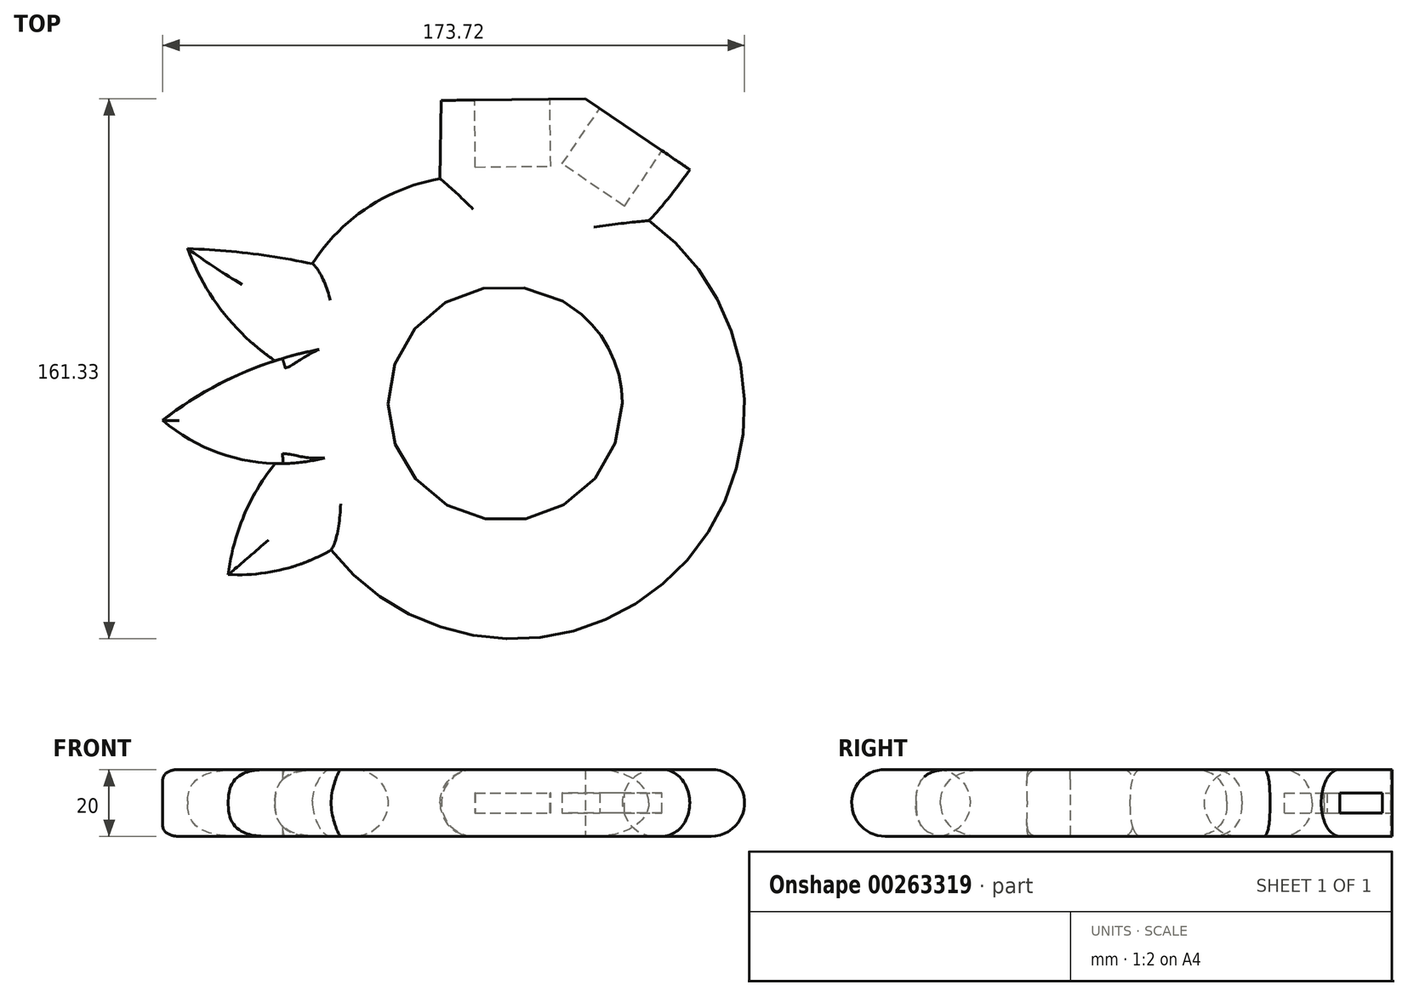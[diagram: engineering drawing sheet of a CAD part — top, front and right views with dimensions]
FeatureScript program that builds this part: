
annotation { "Feature Type Name" : "Feature", "Feature Type Description" : "" }
export const myFeature = defineFeature(function(context is Context, id is Id, definition is map)
    precondition{}
    {
        {
            var Q0;
            Q0=qCreatedBy(makeId("Top.planeOp"),FACE);
            var sketch = newSketch(context, id + "F0", { "sketchPlane" : qUnion([Q0])});
            skArc(sketch, "E0", {"start": v(-69.56, -48.3) * mm, "mid": v(-88.08, -45.25) * mm, "end": v(-106.8, -43.78) * mm});
            skArc(sketch, "E1", {"start": v(-106.8, -43.78) * mm, "mid": v(-96.39, -62.57) * mm, "end": v(-80.73, -77.27) * mm});
            skArc(sketch, "E2", {"start": v(-80.73, -77.27) * mm, "mid": v(-98.26, -84.7) * mm, "end": v(-114.23, -95.07) * mm});
            skArc(sketch, "E3", {"start": v(-114.23, -95.07) * mm, "mid": v(-98.6, -104.41) * mm, "end": v(-80.73, -107.98) * mm});
            skArc(sketch, "E4", {"start": v(-80.73, -107.98) * mm, "mid": v(-90.04, -123.58) * mm, "end": v(-94.69, -141.13) * mm});
            skArc(sketch, "E5", {"start": v(-94.69, -141.13) * mm, "mid": v(-78.8, -139.7) * mm, "end": v(-63.98, -133.8) * mm});
            skArc(sketch, "E6", {"start": v(-63.98, -133.8) * mm, "mid": v(40.14, -139.24) * mm, "end": v(30.94, -35.4) * mm});
            skArc(sketch, "E7", {"start": v(-31.41, -22.87) * mm, "mid": v(-53.17, -31.57) * mm, "end": v(-69.56, -48.3) * mm});
            skCircle(sketch, "E8", {"center": v(-12, -90) * mm, "radius": 35 * mm});
            skLineSegment(sketch, "E9", {"start": v(-12, -90) * mm, "end": v(-12, 0) * mm});
            skLineSegment(sketch, "E10", {"start": v(-12, 0) * mm, "end": v(0, 0) * mm});
            skLineSegment(sketch, "E11", {"start": v(-31.41, -22.87) * mm, "end": v(-12, 0) * mm});
            skLineSegment(sketch, "E12", {"start": v(-31.41, -22.87) * mm, "end": v(0, 0) * mm});
            skArc(sketch, "E13", {"start": v(30.94, -35.4) * mm, "mid": v(57.65, 8.29) * mm, "end": v(64.82, 58.99) * mm});
            skLineSegment(sketch, "E14", {"start": v(64.82, 42.9) * mm, "end": v(70.1, 125.75) * mm});
            skLineSegment(sketch, "E15", {"start": v(70.1, 125.75) * mm, "end": v(73.47, 146.99) * mm});
            skLineSegment(sketch, "E16", {"start": v(73.47, 146.99) * mm, "end": v(91.25, 150.97) * mm});
            skArc(sketch, "E17", {"start": v(93.55, 168.05) * mm, "mid": v(98.13, 170.3) * mm, "end": v(101.04, 174.5) * mm});
            skArc(sketch, "E18", {"start": v(101.04, 174.5) * mm, "mid": v(98.19, 178.86) * mm, "end": v(93.55, 181.22) * mm});
            skArc(sketch, "E19", {"start": v(91.25, 150.97) * mm, "mid": v(97.19, 153.5) * mm, "end": v(101.85, 157.96) * mm});
            skArc(sketch, "E20", {"start": v(101.85, 157.96) * mm, "mid": v(99.5, 164.5) * mm, "end": v(93.55, 168.05) * mm});
            skArc(sketch, "E21", {"start": v(93.55, 181.22) * mm, "mid": v(100.45, 185.24) * mm, "end": v(104.38, 192.2) * mm});
            skArc(sketch, "E22", {"start": v(16.27, 5.35) * mm, "mid": v(27.94, 20.47) * mm, "end": v(35.96, 37.8) * mm});
            skLineSegment(sketch, "E23", {"start": v(16.27, 5.35) * mm, "end": v(12.02, 0.97) * mm});
            skLineSegment(sketch, "E24", {"start": v(12.02, 54.47) * mm, "end": v(16.98, 220.58) * mm});
            skLineSegment(sketch, "E25", {"start": v(16.98, 220.58) * mm, "end": v(16.98, 230.48) * mm});
            skArc(sketch, "E26", {"start": v(20.74, 234.78) * mm, "mid": v(18.05, 233.34) * mm, "end": v(16.98, 230.48) * mm});
            skLineSegment(sketch, "E27", {"start": v(20.74, 234.78) * mm, "end": v(55.67, 234.78) * mm});
            skArc(sketch, "E28", {"start": v(55.67, 234.78) * mm, "mid": v(75.45, 242.82) * mm, "end": v(84, 262.38) * mm});
            skArc(sketch, "E29", {"start": v(84, 262.38) * mm, "mid": v(83.8, 275) * mm, "end": v(79.59, 286.9) * mm});
            skArc(sketch, "E30", {"start": v(79.59, 286.9) * mm, "mid": v(90.12, 305.47) * mm, "end": v(96.46, 325.87) * mm});
            skArc(sketch, "E31", {"start": v(96.46, 325.87) * mm, "mid": v(80.34, 314.22) * mm, "end": v(65.52, 300.95) * mm});
            skArc(sketch, "E32", {"start": v(65.52, 300.95) * mm, "mid": v(66.02, 314.82) * mm, "end": v(65.52, 328.68) * mm});
            skArc(sketch, "E33", {"start": v(41.86, 304.54) * mm, "mid": v(40.03, 315.53) * mm, "end": v(35.9, 325.87) * mm});
            skArc(sketch, "E34", {"start": v(35.9, 325.87) * mm, "mid": v(29.68, 316.4) * mm, "end": v(23.68, 306.81) * mm});
            skArc(sketch, "E35", {"start": v(23.68, 306.81) * mm, "mid": v(-21.12, 284.92) * mm, "end": v(-28, 235.53) * mm});
            skLineSegment(sketch, "E36", {"start": v(-31.41, -22.87) * mm, "end": v(-28, 235.53) * mm});
            skLineSegment(sketch, "E37", {"start": v(0, 0) * mm, "end": v(0, 302.13) * mm});
            skLineSegment(sketch, "E38", {"start": v(12.02, 0.97) * mm, "end": v(-31.41, -22.87) * mm});
            skLineSegment(sketch, "E39", {"start": v(0, 0) * mm, "end": v(12.02, 0.97) * mm});
            skLineSegment(sketch, "E40", {"start": v(12.02, 0.97) * mm, "end": v(30.94, -35.4) * mm});
            skLineSegment(sketch, "E41", {"start": v(64.82, 58.99) * mm, "end": v(46.6, 104.17) * mm});
            skLineSegment(sketch, "E42", {"start": v(12.02, 0.97) * mm, "end": v(12.02, 54.47) * mm});
            skLineSegment(sketch, "E43", {"start": v(-29.54, 119.27) * mm, "end": v(13.94, 118.7) * mm});
            skLineSegment(sketch, "E44", {"start": v(35.96, 37.8) * mm, "end": v(38.97, 138.47) * mm});
            skArc(sketch, "E45", {"start": v(104.38, 192.2) * mm, "mid": v(74.78, 206.52) * mm, "end": v(46.71, 189.39) * mm});
            skArc(sketch, "E46", {"start": v(46.71, 189.39) * mm, "mid": v(41.3, 164.16) * mm, "end": v(38.97, 138.47) * mm});
            skLineSegment(sketch, "E47", {"start": v(104.38, 192.2) * mm, "end": v(93.55, 181.22) * mm});
            skLineSegment(sketch, "E48", {"start": v(93.55, 168.05) * mm, "end": v(101.85, 157.96) * mm});
            skLineSegment(sketch, "E49", {"start": v(93.55, 181.22) * mm, "end": v(101.04, 174.5) * mm});
            skLineSegment(sketch, "E50", {"start": v(93.55, 168.05) * mm, "end": v(101.04, 174.5) * mm});
            skLineSegment(sketch, "E51", {"start": v(41.86, 304.54) * mm, "end": v(65.52, 328.68) * mm});
            skLineSegment(sketch, "E52", {"start": v(16.98, 230.48) * mm, "end": v(-28.07, 230.48) * mm});
            skLineSegment(sketch, "E53", {"start": v(12.02, 0.97) * mm, "end": v(-31.1, 0.49) * mm});
            skPoint(sketch, "E53.endSnap0", {"position": v(6.01, 0.49) * mm});
            skLineSegment(sketch, "E54", {"start": v(12.02, 0.97) * mm, "end": v(43.15, -20.17) * mm});
            skSolve(sketch);
        }
        {
            var Q0;
            {var subQ0=sQuery(id+"F0.wireOp",EDGE,"E38");var subQ1=sQuery(id+"F0.wireOp",EDGE,"E9");var subQ2=makeQuery(id+"F0.imprint","INTERSECT",VERTEX,{"derivedFrom":[subQ1,subQ0]});Q0=makeQuery(id+"F0.imprint","IMPRINT",FACE,{"disambiguationData":[TD([[makeQuery(id+"F0.imprint","IMPRINT",EDGE,{"disambiguationData":[TD([[subQ2,-1.0]])],"derivedFrom":subQ1}),1.0]])]});}
            var Q1;
            {var subQ0=sQuery(id+"F0.wireOp",EDGE,"E11");Q1=makeQuery(id+"F0.imprint","IMPRINT",FACE,{"disambiguationData":[TD([[makeQuery(id+"F0.imprint","IMPRINT",EDGE,{"derivedFrom":subQ0}),-1.0]])]});}
            var Q2;
            {var subQ0=sQuery(id+"F0.wireOp",EDGE,"E39");Q2=makeQuery(id+"F0.imprint","IMPRINT",FACE,{"disambiguationData":[TD([[makeQuery(id+"F0.imprint","IMPRINT",EDGE,{"derivedFrom":subQ0}),1.0]])]});}
            var Q3;
            Q3=makeQuery(id+"F0.imprint","IMPRINT",FACE,{"disambiguationData":[TD([[makeQuery(id+"F0.imprint","IMPRINT",EDGE,{"derivedFrom":sQuery(id+"F0.wireOp",EDGE,"E0")}),1.0]])]});
            var Q4;
            {var subQ5=sQuery(id+"F0.wireOp",EDGE,"E39");Q4=makeQuery(id+"F0.imprint","IMPRINT",FACE,{"disambiguationData":[TD([[makeQuery(id+"F0.imprint","IMPRINT",EDGE,{"derivedFrom":subQ5}),-1.0]])]});}
            var Q5;
            {var subQ2=sQuery(id+"F0.wireOp",EDGE,"E10");Q5=makeQuery(id+"F0.imprint","IMPRINT",FACE,{"disambiguationData":[TD([[makeQuery(id+"F0.imprint","IMPRINT",EDGE,{"derivedFrom":subQ2}),1.0]])]});}
            var Q6;
            {var subQ0=sQuery(id+"F0.wireOp",EDGE,"E10");Q6=makeQuery(id+"F0.imprint","IMPRINT",FACE,{"disambiguationData":[TD([[makeQuery(id+"F0.imprint","IMPRINT",EDGE,{"derivedFrom":subQ0}),-1.0]])]});}
            var Q7;
            {var subQ0=sQuery(id+"F0.wireOp",EDGE,"E40");Q7=makeQuery(id+"F0.imprint","IMPRINT",FACE,{"disambiguationData":[TD([[makeQuery(id+"F0.imprint","IMPRINT",EDGE,{"derivedFrom":subQ0}),1.0]])]});}
            extrude(context, id + "F1", {"entities" : qUnion([Q0, Q1, Q2, Q3, Q4, Q5, Q6, Q7]), "depth" : 20 * mm});
        }
        {
            var Q0;
            {var subQ1=sQuery(id+"F0.wireOp",EDGE,"E14");Q0=makeQuery(id+"F0.imprint","IMPRINT",FACE,{"disambiguationData":[TD([[makeQuery(id+"F0.imprint","IMPRINT",EDGE,{"derivedFrom":subQ1}),1.0]])]});}
            extrude(context, id + "F2", {"entities" : qUnion([Q0]), "depth" : 20 * mm});
        }
        {
            var Q0;
            {var subQ0=sQuery(id+"F0.wireOp",EDGE,"E43");var subQ1=sQuery(id+"F0.wireOp",EDGE,"E36");var subQ2=makeQuery(id+"F0.imprint","INTERSECT",VERTEX,{"derivedFrom":[subQ1,subQ0]});Q0=makeQuery(id+"F0.imprint","IMPRINT",FACE,{"disambiguationData":[TD([[makeQuery(id+"F0.imprint","IMPRINT",EDGE,{"disambiguationData":[TD([[subQ2,1.0]])],"derivedFrom":subQ1}),-1.0]])]});}
            var Q1;
            {var subQ5=sQuery(id+"F0.wireOp",EDGE,"E42");Q1=makeQuery(id+"F0.imprint","IMPRINT",FACE,{"disambiguationData":[TD([[makeQuery(id+"F0.imprint","IMPRINT",EDGE,{"derivedFrom":subQ5}),1.0]])]});}
            var Q2;
            {var subQ0=sQuery(id+"F0.wireOp",EDGE,"E43");var subQ1=sQuery(id+"F0.wireOp",EDGE,"E36");var subQ2=makeQuery(id+"F0.imprint","INTERSECT",VERTEX,{"derivedFrom":[subQ1,subQ0]});Q2=makeQuery(id+"F0.imprint","IMPRINT",FACE,{"disambiguationData":[TD([[makeQuery(id+"F0.imprint","IMPRINT",EDGE,{"disambiguationData":[TD([[subQ2,-1.0]])],"derivedFrom":subQ1}),-1.0]])]});}
            var Q3;
            {var subQ7=sQuery(id+"F0.wireOp",EDGE,"E25");Q3=makeQuery(id+"F0.imprint","IMPRINT",FACE,{"disambiguationData":[TD([[makeQuery(id+"F0.imprint","IMPRINT",EDGE,{"derivedFrom":subQ7}),1.0]])]});}
            extrude(context, id + "F3", {"entities" : qUnion([Q0, Q1, Q2, Q3]), "depth" : 20 * mm});
        }
        {
            var Q0;
            {var subQ0=sQuery(id+"F0.wireOp",EDGE,"E36");var subQ1=sQuery(id+"F0.wireOp",EDGE,"E35");var subQ2=makeQuery(id+"F0.imprint","INTERSECT",VERTEX,{"derivedFrom":[subQ1,subQ0]});Q0=makeQuery(id+"F0.imprint","IMPRINT",FACE,{"disambiguationData":[TD([[makeQuery(id+"F0.imprint","IMPRINT",EDGE,{"disambiguationData":[TD([[subQ2,1.0]])],"derivedFrom":subQ1}),1.0]])]});}
            var Q1;
            {var subQ4=sQuery(id+"F0.wireOp",EDGE,"E26");Q1=makeQuery(id+"F0.imprint","IMPRINT",FACE,{"disambiguationData":[TD([[makeQuery(id+"F0.imprint","IMPRINT",EDGE,{"derivedFrom":subQ4}),-1.0]])]});}
            extrude(context, id + "F4", {"entities" : qUnion([Q0, Q1]), "depth" : 20 * mm});
        }
        {
            var Q0;
            Q0=makeQuery(id+"F1.opExtrude","CAP_EDGE",EDGE,{"disambiguationData":[OSD([sQuery(id+"F0.wireOp",EDGE,"E36")])],"isStart":false});
            var Q1;
            Q1=makeQuery(id+"F1.opExtrude","CAP_EDGE",EDGE,{"disambiguationData":[OSD([sQuery(id+"F0.wireOp",EDGE,"E24")])],"isStart":false});
            var Q2;
            Q2=makeQuery(id+"F1.opExtrude","CAP_EDGE",EDGE,{"disambiguationData":[OSD([sQuery(id+"F0.wireOp",EDGE,"E42")])],"isStart":false});
            var Q3;
            Q3=makeQuery(id+"F1.opExtrude","CAP_EDGE",EDGE,{"disambiguationData":[OSD([sQuery(id+"F0.wireOp",EDGE,"E25")])],"isStart":false});
            var Q4;
            Q4=makeQuery(id+"F1.opExtrude","CAP_EDGE",EDGE,{"disambiguationData":[OSD([sQuery(id+"F0.wireOp",EDGE,"E35")])],"isStart":false});
            var Q5;
            Q5=makeQuery(id+"F1.opExtrude","CAP_EDGE",EDGE,{"disambiguationData":[OSD([sQuery(id+"F0.wireOp",EDGE,"E26")])],"isStart":false});
            var Q6;
            Q6=makeQuery(id+"F1.opExtrude","CAP_EDGE",EDGE,{"disambiguationData":[OSD([sQuery(id+"F0.wireOp",EDGE,"E42")])],"isStart":true});
            var Q7;
            Q7=makeQuery(id+"F1.opExtrude","CAP_EDGE",EDGE,{"disambiguationData":[OSD([sQuery(id+"F0.wireOp",EDGE,"E25")])],"isStart":true});
            var Q8;
            Q8=makeQuery(id+"F1.opExtrude","CAP_EDGE",EDGE,{"disambiguationData":[OSD([sQuery(id+"F0.wireOp",EDGE,"E36")])],"isStart":true});
            var Q9;
            Q9=makeQuery(id+"F1.opExtrude","CAP_EDGE",EDGE,{"disambiguationData":[OSD([sQuery(id+"F0.wireOp",EDGE,"E35")])],"isStart":true});
            var Q10;
            Q10=makeQuery(id+"F1.opExtrude","CAP_EDGE",EDGE,{"disambiguationData":[OSD([sQuery(id+"F0.wireOp",EDGE,"E26")])],"isStart":true});
            var Q11;
            Q11=makeQuery(id+"F1.opExtrude","CAP_EDGE",EDGE,{"disambiguationData":[OSD([sQuery(id+"F0.wireOp",EDGE,"E22")])],"isStart":false});
            var Q12;
            Q12=makeQuery(id+"F1.opExtrude","CAP_EDGE",EDGE,{"disambiguationData":[OSD([sQuery(id+"F0.wireOp",EDGE,"E23")])],"isStart":false});
            var Q13;
            Q13=makeQuery(id+"F1.opExtrude","CAP_EDGE",EDGE,{"disambiguationData":[OSD([sQuery(id+"F0.wireOp",EDGE,"E44")])],"isStart":false});
            var Q14;
            Q14=makeQuery(id+"F1.opExtrude","CAP_EDGE",EDGE,{"disambiguationData":[OSD([sQuery(id+"F0.wireOp",EDGE,"E45")])],"isStart":false});
            var Q15;
            Q15=makeQuery(id+"F1.opExtrude","CAP_EDGE",EDGE,{"disambiguationData":[OSD([sQuery(id+"F0.wireOp",EDGE,"E22")])],"isStart":true});
            var Q16;
            Q16=makeQuery(id+"F1.opExtrude","CAP_EDGE",EDGE,{"disambiguationData":[OSD([sQuery(id+"F0.wireOp",EDGE,"E44")])],"isStart":true});
            var Q17;
            Q17=makeQuery(id+"F1.opExtrude","CAP_EDGE",EDGE,{"disambiguationData":[OSD([sQuery(id+"F0.wireOp",EDGE,"E45")])],"isStart":true});
            var Q18;
            Q18=makeQuery(id+"F1.opExtrude","CAP_EDGE",EDGE,{"disambiguationData":[OSD([sQuery(id+"F0.wireOp",EDGE,"E13")])],"isStart":false});
            var Q19;
            Q19=makeQuery(id+"F1.opExtrude","CAP_EDGE",EDGE,{"disambiguationData":[OSD([sQuery(id+"F0.wireOp",EDGE,"E14")])],"isStart":false});
            var Q20;
            Q20=makeQuery(id+"F1.opExtrude","CAP_EDGE",EDGE,{"disambiguationData":[OSD([sQuery(id+"F0.wireOp",EDGE,"E15")])],"isStart":false});
            var Q21;
            Q21=makeQuery(id+"F1.opExtrude","CAP_EDGE",EDGE,{"disambiguationData":[OSD([sQuery(id+"F0.wireOp",EDGE,"E16")])],"isStart":false});
            var Q22;
            Q22=makeQuery(id+"F1.opExtrude","CAP_EDGE",EDGE,{"disambiguationData":[OSD([sQuery(id+"F0.wireOp",EDGE,"E16")])],"isStart":true});
            var Q23;
            Q23=makeQuery(id+"F1.opExtrude","CAP_EDGE",EDGE,{"disambiguationData":[OSD([sQuery(id+"F0.wireOp",EDGE,"E15")])],"isStart":true});
            var Q24;
            Q24=makeQuery(id+"F1.opExtrude","CAP_EDGE",EDGE,{"disambiguationData":[OSD([sQuery(id+"F0.wireOp",EDGE,"E14")])],"isStart":true});
            var Q25;
            Q25=makeQuery(id+"F1.opExtrude","CAP_EDGE",EDGE,{"disambiguationData":[OSD([sQuery(id+"F0.wireOp",EDGE,"E13")])],"isStart":true});
            var Q26;
            Q26=makeQuery(id+"F1.opExtrude","CAP_EDGE",EDGE,{"disambiguationData":[OSD([sQuery(id+"F0.wireOp",EDGE,"E6")])],"isStart":false});
            var Q27;
            Q27=makeQuery(id+"F1.opExtrude","CAP_EDGE",EDGE,{"disambiguationData":[OSD([sQuery(id+"F0.wireOp",EDGE,"E8")])],"isStart":false});
            var Q28;
            Q28=makeQuery(id+"F1.opExtrude","CAP_EDGE",EDGE,{"disambiguationData":[OSD([sQuery(id+"F0.wireOp",EDGE,"E7")])],"isStart":false});
            var Q29;
            Q29=makeQuery(id+"F1.opExtrude","CAP_EDGE",EDGE,{"disambiguationData":[OSD([sQuery(id+"F0.wireOp",EDGE,"E8")])],"isStart":true});
            var Q30;
            Q30=makeQuery(id+"F1.opExtrude","CAP_EDGE",EDGE,{"disambiguationData":[OSD([sQuery(id+"F0.wireOp",EDGE,"E7")])],"isStart":true});
            var Q31;
            Q31=makeQuery(id+"F1.opExtrude","CAP_EDGE",EDGE,{"disambiguationData":[OSD([sQuery(id+"F0.wireOp",EDGE,"E6")])],"isStart":true});
            fillet(context, id + "F5", {"entities" : qUnion([Q0, Q1, Q2, Q3, Q4, Q5, Q6, Q7, Q8, Q9, Q10, Q11, Q12, Q13, Q14, Q15, Q16, Q17, Q18, Q19, Q20, Q21, Q22, Q23, Q24, Q25, Q26, Q27, Q28, Q29, Q30, Q31]), "radius" : 10 * mm, "tangentPropagation" : true, "allowEdgeOverflow" : false});
        }
        {
            var Q0;
            Q0=makeQuery(id+"F1.opExtrude","CAP_EDGE",EDGE,{"disambiguationData":[OSD([sQuery(id+"F0.wireOp",EDGE,"E0")])],"isStart":false});
            var Q1;
            Q1=makeQuery(id+"F1.opExtrude","CAP_EDGE",EDGE,{"disambiguationData":[OSD([sQuery(id+"F0.wireOp",EDGE,"E1")])],"isStart":false});
            var Q2;
            Q2=makeQuery(id+"F1.opExtrude","CAP_EDGE",EDGE,{"disambiguationData":[OSD([sQuery(id+"F0.wireOp",EDGE,"E5")])],"isStart":false});
            var Q3;
            Q3=makeQuery(id+"F1.opExtrude","CAP_EDGE",EDGE,{"disambiguationData":[OSD([sQuery(id+"F0.wireOp",EDGE,"E4")])],"isStart":false});
            var Q4;
            Q4=makeQuery(id+"F1.opExtrude","CAP_EDGE",EDGE,{"disambiguationData":[OSD([sQuery(id+"F0.wireOp",EDGE,"E0")])],"isStart":true});
            var Q5;
            Q5=makeQuery(id+"F1.opExtrude","CAP_EDGE",EDGE,{"disambiguationData":[OSD([sQuery(id+"F0.wireOp",EDGE,"E1")])],"isStart":true});
            var Q6;
            Q6=makeQuery(id+"F1.opExtrude","CAP_EDGE",EDGE,{"disambiguationData":[OSD([sQuery(id+"F0.wireOp",EDGE,"E4")])],"isStart":true});
            var Q7;
            Q7=makeQuery(id+"F1.opExtrude","CAP_EDGE",EDGE,{"disambiguationData":[OSD([sQuery(id+"F0.wireOp",EDGE,"E5")])],"isStart":true});
            fillet(context, id + "F6", {"entities" : qUnion([Q0, Q1, Q2, Q3, Q4, Q5, Q6, Q7]), "radius" : 9.5 * mm, "tangentPropagation" : true, "rho" : 0.5, "crossSection" : FilletCrossSection.CONIC, "allowEdgeOverflow" : false});
        }
        {
            var Q0;
            Q0=makeQuery(id+"F1.opExtrude","CAP_EDGE",EDGE,{"disambiguationData":[OSD([sQuery(id+"F0.wireOp",EDGE,"E3")])],"isStart":true});
            var Q1;
            Q1=makeQuery(id+"F1.opExtrude","CAP_EDGE",EDGE,{"disambiguationData":[OSD([sQuery(id+"F0.wireOp",EDGE,"E2")])],"isStart":true});
            var Q2;
            Q2=makeQuery(id+"F1.opExtrude","CAP_EDGE",EDGE,{"disambiguationData":[OSD([sQuery(id+"F0.wireOp",EDGE,"E2")])],"isStart":false});
            var Q3;
            Q3=makeQuery(id+"F1.opExtrude","CAP_EDGE",EDGE,{"disambiguationData":[OSD([sQuery(id+"F0.wireOp",EDGE,"E3")])],"isStart":false});
            fillet(context, id + "F7", {"entities" : qUnion([Q0, Q1, Q2, Q3]), "radius" : 3 * mm, "tangentPropagation" : true, "allowEdgeOverflow" : false});
        }
        {
            var Q0;
            Q0=makeQuery(id+"F2.opExtrude","CAP_EDGE",EDGE,{"disambiguationData":[OSD([sQuery(id+"F0.wireOp",EDGE,"E14")])],"isStart":false});
            var Q1;
            Q1=makeQuery(id+"F2.opExtrude","CAP_EDGE",EDGE,{"disambiguationData":[OSD([sQuery(id+"F0.wireOp",EDGE,"E15")])],"isStart":false});
            var Q2;
            Q2=makeQuery(id+"F2.opExtrude","CAP_EDGE",EDGE,{"disambiguationData":[OSD([sQuery(id+"F0.wireOp",EDGE,"E14")])],"isStart":true});
            var Q3;
            Q3=makeQuery(id+"F2.opExtrude","CAP_EDGE",EDGE,{"disambiguationData":[OSD([sQuery(id+"F0.wireOp",EDGE,"E15")])],"isStart":true});
            var Q4;
            Q4=makeQuery(id+"F2.opExtrude","CAP_EDGE",EDGE,{"disambiguationData":[OSD([sQuery(id+"F0.wireOp",EDGE,"E16")])],"isStart":true});
            var Q5;
            Q5=makeQuery(id+"F2.opExtrude","CAP_EDGE",EDGE,{"disambiguationData":[OSD([sQuery(id+"F0.wireOp",EDGE,"E16")])],"isStart":false});
            var Q6;
            Q6=makeQuery(id+"F2.opExtrude","CAP_EDGE",EDGE,{"disambiguationData":[OSD([sQuery(id+"F0.wireOp",EDGE,"E45")])],"isStart":true});
            var Q7;
            Q7=makeQuery(id+"F2.opExtrude","CAP_EDGE",EDGE,{"disambiguationData":[OSD([sQuery(id+"F0.wireOp",EDGE,"E45")])],"isStart":false});
            var Q8;
            Q8=makeQuery(id+"F2.opExtrude","CAP_EDGE",EDGE,{"disambiguationData":[OSD([sQuery(id+"F0.wireOp",EDGE,"E46")])],"isStart":false});
            var Q9;
            Q9=makeQuery(id+"F2.opExtrude","CAP_EDGE",EDGE,{"disambiguationData":[OSD([sQuery(id+"F0.wireOp",EDGE,"E44")])],"isStart":false});
            var Q10;
            Q10=makeQuery(id+"F2.opExtrude","CAP_EDGE",EDGE,{"disambiguationData":[OSD([sQuery(id+"F0.wireOp",EDGE,"E22")])],"isStart":false});
            var Q11;
            Q11=makeQuery(id+"F2.opExtrude","CAP_EDGE",EDGE,{"disambiguationData":[OSD([sQuery(id+"F0.wireOp",EDGE,"E23")])],"isStart":false});
            var Q12;
            Q12=makeQuery(id+"F2.opExtrude","CAP_EDGE",EDGE,{"disambiguationData":[OSD([sQuery(id+"F0.wireOp",EDGE,"E46")])],"isStart":true});
            var Q13;
            Q13=makeQuery(id+"F2.opExtrude","CAP_EDGE",EDGE,{"disambiguationData":[OSD([sQuery(id+"F0.wireOp",EDGE,"E23")])],"isStart":true});
            var Q14;
            Q14=makeQuery(id+"F2.opExtrude","CAP_EDGE",EDGE,{"disambiguationData":[OSD([sQuery(id+"F0.wireOp",EDGE,"E22")])],"isStart":true});
            var Q15;
            Q15=makeQuery(id+"F2.opExtrude","CAP_EDGE",EDGE,{"disambiguationData":[OSD([sQuery(id+"F0.wireOp",EDGE,"E44")])],"isStart":true});
            var Q16;
            Q16=makeQuery(id+"F3.opExtrude","CAP_EDGE",EDGE,{"disambiguationData":[OSD([sQuery(id+"F0.wireOp",EDGE,"E24")])],"isStart":false});
            var Q17;
            Q17=makeQuery(id+"F3.opExtrude","CAP_EDGE",EDGE,{"disambiguationData":[OSD([sQuery(id+"F0.wireOp",EDGE,"E42")])],"isStart":false});
            var Q18;
            Q18=makeQuery(id+"F3.opExtrude","CAP_EDGE",EDGE,{"disambiguationData":[OSD([sQuery(id+"F0.wireOp",EDGE,"E42")])],"isStart":true});
            var Q19;
            Q19=makeQuery(id+"F3.opExtrude","CAP_EDGE",EDGE,{"disambiguationData":[OSD([sQuery(id+"F0.wireOp",EDGE,"E24")])],"isStart":true});
            var Q20;
            Q20=makeQuery(id+"F3.opExtrude","CAP_EDGE",EDGE,{"disambiguationData":[OSD([sQuery(id+"F0.wireOp",EDGE,"E25")])],"isStart":true});
            var Q21;
            Q21=makeQuery(id+"F3.opExtrude","CAP_EDGE",EDGE,{"disambiguationData":[OSD([sQuery(id+"F0.wireOp",EDGE,"E36")])],"isStart":false});
            var Q22;
            Q22=makeQuery(id+"F3.opExtrude","CAP_EDGE",EDGE,{"disambiguationData":[OSD([sQuery(id+"F0.wireOp",EDGE,"E36")])],"isStart":true});
            var Q23;
            Q23=makeQuery(id+"F4.opExtrude","CAP_EDGE",EDGE,{"disambiguationData":[OSD([sQuery(id+"F0.wireOp",EDGE,"E36")])],"isStart":true});
            var Q24;
            Q24=makeQuery(id+"F4.opExtrude","CAP_EDGE",EDGE,{"disambiguationData":[OSD([sQuery(id+"F0.wireOp",EDGE,"E36")])],"isStart":false});
            var Q25;
            Q25=makeQuery(id+"F4.opExtrude","CAP_EDGE",EDGE,{"disambiguationData":[OSD([sQuery(id+"F0.wireOp",EDGE,"E35")])],"isStart":true});
            var Q26;
            Q26=makeQuery(id+"F4.opExtrude","CAP_EDGE",EDGE,{"disambiguationData":[OSD([sQuery(id+"F0.wireOp",EDGE,"E35")])],"isStart":false});
            var Q27;
            Q27=makeQuery(id+"F4.opExtrude","CAP_EDGE",EDGE,{"disambiguationData":[OSD([sQuery(id+"F0.wireOp",EDGE,"E27")])],"isStart":false});
            var Q28;
            Q28=makeQuery(id+"F4.opExtrude","CAP_EDGE",EDGE,{"disambiguationData":[OSD([sQuery(id+"F0.wireOp",EDGE,"E28")])],"isStart":false});
            var Q29;
            Q29=makeQuery(id+"F4.opExtrude","CAP_EDGE",EDGE,{"disambiguationData":[OSD([sQuery(id+"F0.wireOp",EDGE,"E29")])],"isStart":false});
            var Q30;
            Q30=makeQuery(id+"F4.opExtrude","CAP_EDGE",EDGE,{"disambiguationData":[OSD([sQuery(id+"F0.wireOp",EDGE,"E27")])],"isStart":true});
            var Q31;
            Q31=makeQuery(id+"F4.opExtrude","CAP_EDGE",EDGE,{"disambiguationData":[OSD([sQuery(id+"F0.wireOp",EDGE,"E28")])],"isStart":true});
            var Q32;
            Q32=makeQuery(id+"F4.opExtrude","CAP_EDGE",EDGE,{"disambiguationData":[OSD([sQuery(id+"F0.wireOp",EDGE,"E29")])],"isStart":true});
            var Q33;
            Q33=makeQuery(id+"F4.opExtrude","CAP_EDGE",EDGE,{"disambiguationData":[OSD([sQuery(id+"F0.wireOp",EDGE,"E26")])],"isStart":false});
            var Q34;
            Q34=makeQuery(id+"F4.opExtrude","CAP_EDGE",EDGE,{"disambiguationData":[OSD([sQuery(id+"F0.wireOp",EDGE,"E26")])],"isStart":true});
            var Q35;
            Q35=makeQuery(id+"F4.opExtrude","CAP_EDGE",EDGE,{"disambiguationData":[OSD([sQuery(id+"F0.wireOp",EDGE,"E30")])],"isStart":false});
            var Q36;
            Q36=makeQuery(id+"F4.opExtrude","CAP_EDGE",EDGE,{"disambiguationData":[OSD([sQuery(id+"F0.wireOp",EDGE,"E31")])],"isStart":false});
            var Q37;
            Q37=makeQuery(id+"F4.opExtrude","CAP_EDGE",EDGE,{"disambiguationData":[OSD([sQuery(id+"F0.wireOp",EDGE,"E30")])],"isStart":true});
            var Q38;
            Q38=makeQuery(id+"F4.opExtrude","CAP_EDGE",EDGE,{"disambiguationData":[OSD([sQuery(id+"F0.wireOp",EDGE,"E31")])],"isStart":true});
            var Q39;
            Q39=makeQuery(id+"F4.opExtrude","CAP_EDGE",EDGE,{"disambiguationData":[OSD([sQuery(id+"F0.wireOp",EDGE,"E33")])],"isStart":false});
            var Q40;
            Q40=makeQuery(id+"F4.opExtrude","CAP_EDGE",EDGE,{"disambiguationData":[OSD([sQuery(id+"F0.wireOp",EDGE,"E34")])],"isStart":false});
            var Q41;
            Q41=makeQuery(id+"F4.opExtrude","CAP_EDGE",EDGE,{"disambiguationData":[OSD([sQuery(id+"F0.wireOp",EDGE,"E34")])],"isStart":true});
            var Q42;
            Q42=makeQuery(id+"F4.opExtrude","CAP_EDGE",EDGE,{"disambiguationData":[OSD([sQuery(id+"F0.wireOp",EDGE,"E33")])],"isStart":true});
            fillet(context, id + "F8", {"entities" : qUnion([Q0, Q1, Q2, Q3, Q4, Q5, Q6, Q7, Q8, Q9, Q10, Q11, Q12, Q13, Q14, Q15, Q16, Q17, Q18, Q19, Q20, Q21, Q22, Q23, Q24, Q25, Q26, Q27, Q28, Q29, Q30, Q31, Q32, Q33, Q34, Q35, Q36, Q37, Q38, Q39, Q40, Q41, Q42]), "radius" : 10 * mm, "tangentPropagation" : true, "allowEdgeOverflow" : false});
        }
        {
            var Q0;
            Q0=makeQuery(id+"F4.opExtrude","CAP_EDGE",EDGE,{"disambiguationData":[OSD([sQuery(id+"F0.wireOp",EDGE,"E51")])],"isStart":false});
            var Q1;
            Q1=makeQuery(id+"F4.opExtrude","CAP_EDGE",EDGE,{"disambiguationData":[OSD([sQuery(id+"F0.wireOp",EDGE,"E32")])],"isStart":false});
            var Q2;
            Q2=makeQuery(id+"F4.opExtrude","CAP_EDGE",EDGE,{"disambiguationData":[OSD([sQuery(id+"F0.wireOp",EDGE,"E32")])],"isStart":true});
            var Q3;
            Q3=makeQuery(id+"F4.opExtrude","CAP_EDGE",EDGE,{"disambiguationData":[OSD([sQuery(id+"F0.wireOp",EDGE,"E51")])],"isStart":true});
            fillet(context, id + "F9", {"entities" : qUnion([Q0, Q1, Q2, Q3]), "radius" : 5 * mm, "tangentPropagation" : true, "allowEdgeOverflow" : false});
        }
        {
            var Q0;
            Q0=makeQuery(id+"F2.opExtrude","CAP_EDGE",EDGE,{"disambiguationData":[OSD([sQuery(id+"F0.wireOp",EDGE,"E50")])],"isStart":true});
            var Q1;
            Q1=makeQuery(id+"F2.opExtrude","CAP_EDGE",EDGE,{"disambiguationData":[OSD([sQuery(id+"F0.wireOp",EDGE,"E49")])],"isStart":true});
            var Q2;
            Q2=makeQuery(id+"F2.opExtrude","CAP_EDGE",EDGE,{"disambiguationData":[OSD([sQuery(id+"F0.wireOp",EDGE,"E49")])],"isStart":false});
            var Q3;
            Q3=makeQuery(id+"F2.opExtrude","CAP_EDGE",EDGE,{"disambiguationData":[OSD([sQuery(id+"F0.wireOp",EDGE,"E50")])],"isStart":false});
            var Q4;
            Q4=makeQuery(id+"F8.opFillet","BLEND_EDGE",EDGE,{"blendedFrom":[makeQuery(id+"F2.opExtrude","CAP_EDGE",EDGE,{"disambiguationData":[OSD([sQuery(id+"F0.wireOp",EDGE,"E45")])],"isStart":false}),makeQuery(id+"F2.opExtrude","SWEPT_FACE",FACE,{"disambiguationData":[OSD([sQuery(id+"F0.wireOp",EDGE,"E47")])]})],"blendedInto":[makeQuery(id+"F2.opExtrude","SWEPT_FACE",FACE,{"disambiguationData":[OSD([sQuery(id+"F0.wireOp",EDGE,"E47")])]})]});
            var Q5;
            Q5=makeQuery(id+"F8.opFillet","BLEND_EDGE",EDGE,{"blendedFrom":[makeQuery(id+"F2.opExtrude","CAP_EDGE",EDGE,{"disambiguationData":[OSD([sQuery(id+"F0.wireOp",EDGE,"E19")])],"isStart":false}),makeQuery(id+"F2.opExtrude","SWEPT_FACE",FACE,{"disambiguationData":[OSD([sQuery(id+"F0.wireOp",EDGE,"E48")])]})],"blendedInto":[makeQuery(id+"F2.opExtrude","SWEPT_FACE",FACE,{"disambiguationData":[OSD([sQuery(id+"F0.wireOp",EDGE,"E48")])]})]});
            fillet(context, id + "F10", {"entities" : qUnion([Q0, Q1, Q2, Q3, Q4, Q5]), "radius" : 5 * mm, "tangentPropagation" : true, "allowEdgeOverflow" : false});
        }
        {
            var Q0;
            Q0=makeQuery(id+"F5.opFillet","SPLIT",FACE,{"disambiguationData":[OD(0.0)],"derivedFrom":makeQuery(id+"F1.opExtrude","CAP_FACE",FACE,{"disambiguationData":[OSD([sQuery(id+"F0.wireOp",EDGE,"E0"),sQuery(id+"F0.wireOp",EDGE,"E1"),sQuery(id+"F0.wireOp",EDGE,"E2"),sQuery(id+"F0.wireOp",EDGE,"E3"),sQuery(id+"F0.wireOp",EDGE,"E4"),sQuery(id+"F0.wireOp",EDGE,"E5"),sQuery(id+"F0.wireOp",EDGE,"E6"),sQuery(id+"F0.wireOp",EDGE,"E7"),sQuery(id+"F0.wireOp",EDGE,"E8"),sQuery(id+"F0.wireOp",EDGE,"E13"),sQuery(id+"F0.wireOp",EDGE,"E14"),sQuery(id+"F0.wireOp",EDGE,"E15"),sQuery(id+"F0.wireOp",EDGE,"E16"),sQuery(id+"F0.wireOp",EDGE,"E19"),sQuery(id+"F0.wireOp",EDGE,"E22"),sQuery(id+"F0.wireOp",EDGE,"E23"),sQuery(id+"F0.wireOp",EDGE,"E24"),sQuery(id+"F0.wireOp",EDGE,"E25"),sQuery(id+"F0.wireOp",EDGE,"E26"),sQuery(id+"F0.wireOp",EDGE,"E27"),sQuery(id+"F0.wireOp",EDGE,"E28"),sQuery(id+"F0.wireOp",EDGE,"E29"),sQuery(id+"F0.wireOp",EDGE,"E30"),sQuery(id+"F0.wireOp",EDGE,"E31"),sQuery(id+"F0.wireOp",EDGE,"E32"),sQuery(id+"F0.wireOp",EDGE,"E33"),sQuery(id+"F0.wireOp",EDGE,"E34"),sQuery(id+"F0.wireOp",EDGE,"E35"),sQuery(id+"F0.wireOp",EDGE,"E36"),sQuery(id+"F0.wireOp",EDGE,"E42"),sQuery(id+"F0.wireOp",EDGE,"E44"),sQuery(id+"F0.wireOp",EDGE,"E45"),sQuery(id+"F0.wireOp",EDGE,"E46"),sQuery(id+"F0.wireOp",EDGE,"E47"),sQuery(id+"F0.wireOp",EDGE,"E48"),sQuery(id+"F0.wireOp",EDGE,"E49"),sQuery(id+"F0.wireOp",EDGE,"E50"),sQuery(id+"F0.wireOp",EDGE,"E51")])],"isStart":false})});
            var sketch = newSketch(context, id + "F11", { "sketchPlane" : qUnion([Q0])});
            skLineSegment(sketch, "E55", {"start": v(0, 0) * mm, "end": v(3.83, 289.97) * mm});
            skLineSegment(sketch, "E56", {"start": v(3.83, 289.97) * mm, "end": v(19.83, 289.76) * mm});
            skCircle(sketch, "E57", {"center": v(19.83, 289.76) * mm, "radius": 10 * mm});
            skSolve(sketch);
        }
        {
            var Q0;
            Q0=makeQuery(id+"F11.imprint","IMPRINT",FACE,{"disambiguationData":[TD([[makeQuery(id+"F11.imprint","IMPRINT",EDGE,{"derivedFrom":sQuery(id+"F11.wireOp",EDGE,"E57")}),1.0]])]});
            extrude(context, id + "F12", {"entities" : qUnion([Q0]), "operationType" : NewBodyOperationType.ADD, "depth" : 5 * mm, "hasSecondDirection" : true, "secondDirectionOppositeDirection" : true, "secondDirectionDepth" : 25 * mm});
        }
        {
            var Q0;
            Q0=makeQuery(id+"F12.opExtrude","CAP_EDGE",EDGE,{"disambiguationData":[OSD([sQuery(id+"F11.wireOp",EDGE,"E57")])],"isStart":false});
            chamfer(context, id + "F13", {"entities" : qUnion([Q0]), "chamferType" : ChamferType.OFFSET_ANGLE, "width" : 7 * mm, "oppositeDirection" : false, "angle" : 30 * degree, "tangentPropagation" : true});
        }
        {
            var Q0;
            Q0=makeQuery(id+"F12.opExtrude","CAP_EDGE",EDGE,{"disambiguationData":[OSD([sQuery(id+"F11.wireOp",EDGE,"E57")])],"isStart":true});
            chamfer(context, id + "F14", {"entities" : qUnion([Q0]), "chamferType" : ChamferType.OFFSET_ANGLE, "width" : 4 * mm, "oppositeDirection" : false, "angle" : 60 * degree, "tangentPropagation" : true});
        }
        {
            var Q0;
            Q0=makeQuery(id+"F2.opExtrude","SWEPT_BODY",BODY,{"disambiguationData":[OSD([sQuery(id+"F0.wireOp",EDGE,"E13"),sQuery(id+"F0.wireOp",EDGE,"E14"),sQuery(id+"F0.wireOp",EDGE,"E15"),sQuery(id+"F0.wireOp",EDGE,"E16"),sQuery(id+"F0.wireOp",EDGE,"E19"),sQuery(id+"F0.wireOp",EDGE,"E22"),sQuery(id+"F0.wireOp",EDGE,"E23"),sQuery(id+"F0.wireOp",EDGE,"E44"),sQuery(id+"F0.wireOp",EDGE,"E45"),sQuery(id+"F0.wireOp",EDGE,"E46"),sQuery(id+"F0.wireOp",EDGE,"E47"),sQuery(id+"F0.wireOp",EDGE,"E48"),sQuery(id+"F0.wireOp",EDGE,"E49"),sQuery(id+"F0.wireOp",EDGE,"E50"),sQuery(id+"F0.wireOp",EDGE,"E54")])]});
            deleteBodies(context, id + "F15", {"entities" : qUnion([Q0])});
        }
        {
            var Q0;
            Q0=makeQuery(id+"F3.opExtrude","SWEPT_BODY",BODY,{"disambiguationData":[OSD([sQuery(id+"F0.wireOp",EDGE,"E24"),sQuery(id+"F0.wireOp",EDGE,"E25"),sQuery(id+"F0.wireOp",EDGE,"E36"),sQuery(id+"F0.wireOp",EDGE,"E42"),sQuery(id+"F0.wireOp",EDGE,"E52"),sQuery(id+"F0.wireOp",EDGE,"E53")])]});
            deleteBodies(context, id + "F16", {"entities" : qUnion([Q0])});
        }
        {
            var Q0;
            Q0=makeQuery(id+"F4.opExtrude","SWEPT_BODY",BODY,{"disambiguationData":[OSD([sQuery(id+"F0.wireOp",EDGE,"E26"),sQuery(id+"F0.wireOp",EDGE,"E27"),sQuery(id+"F0.wireOp",EDGE,"E28"),sQuery(id+"F0.wireOp",EDGE,"E29"),sQuery(id+"F0.wireOp",EDGE,"E30"),sQuery(id+"F0.wireOp",EDGE,"E31"),sQuery(id+"F0.wireOp",EDGE,"E32"),sQuery(id+"F0.wireOp",EDGE,"E33"),sQuery(id+"F0.wireOp",EDGE,"E34"),sQuery(id+"F0.wireOp",EDGE,"E35"),sQuery(id+"F0.wireOp",EDGE,"E36"),sQuery(id+"F0.wireOp",EDGE,"E51"),sQuery(id+"F0.wireOp",EDGE,"E52")])]});
            deleteBodies(context, id + "F17", {"entities" : qUnion([Q0])});
        }
        {
            var Q0;
            Q0=makeQuery(id+"F1.opExtrude","SWEPT_FACE",FACE,{"disambiguationData":[OSD([sQuery(id+"F0.wireOp",EDGE,"E53")])]});
            var sketch = newSketch(context, id + "F18", { "sketchPlane" : qUnion([Q0])});
            skLineSegment(sketch, "E58", {"start": v(31.1, 10) * mm, "end": v(21.1, 10) * mm});
            skLineSegment(sketch, "E59", {"start": v(21.1, 10) * mm, "end": v(21.1, 7) * mm});
            skLineSegment(sketch, "E60.bottom", {"start": v(21.1, 7) * mm, "end": v(-1.4, 7) * mm});
            skLineSegment(sketch, "E60.top", {"start": v(21.1, 13) * mm, "end": v(-1.4, 13) * mm});
            skLineSegment(sketch, "E60.left", {"start": v(21.1, 7) * mm, "end": v(21.1, 13) * mm});
            skLineSegment(sketch, "E60.right", {"start": v(-1.4, 7) * mm, "end": v(-1.4, 13) * mm});
            skSolve(sketch);
        }
        {
            var Q0;
            Q0 = qSketchRegion(id + "F18", true);
            extrude(context, id + "F19", {"entities" : qUnion([Q0]), "operationType" : NewBodyOperationType.REMOVE, "oppositeDirection" : true, "depth" : 20 * mm});
        }
        {
            var Q0;
            Q0=makeQuery(id+"F1.opExtrude","SWEPT_FACE",FACE,{"disambiguationData":[OSD([sQuery(id+"F0.wireOp",EDGE,"E54")])]});
            var sketch = newSketch(context, id + "F20", { "sketchPlane" : qUnion([Q0])});
            skLineSegment(sketch, "E61", {"start": v(-47.03, 10) * mm, "end": v(-37.03, 10) * mm});
            skLineSegment(sketch, "E62", {"start": v(-37.03, 10) * mm, "end": v(-37.03, 13) * mm});
            skLineSegment(sketch, "E63.bottom", {"start": v(-37.03, 13) * mm, "end": v(-14.53, 13) * mm});
            skLineSegment(sketch, "E63.top", {"start": v(-37.03, 7) * mm, "end": v(-14.53, 7) * mm});
            skLineSegment(sketch, "E63.left", {"start": v(-37.03, 13) * mm, "end": v(-37.03, 7) * mm});
            skLineSegment(sketch, "E63.right", {"start": v(-14.53, 13) * mm, "end": v(-14.53, 7) * mm});
            skSolve(sketch);
        }
        {
            var Q0;
            Q0 = qSketchRegion(id + "F20", true);
            extrude(context, id + "F21", {"entities" : qUnion([Q0]), "operationType" : NewBodyOperationType.REMOVE, "oppositeDirection" : true, "depth" : 20 * mm});
        }
    });
